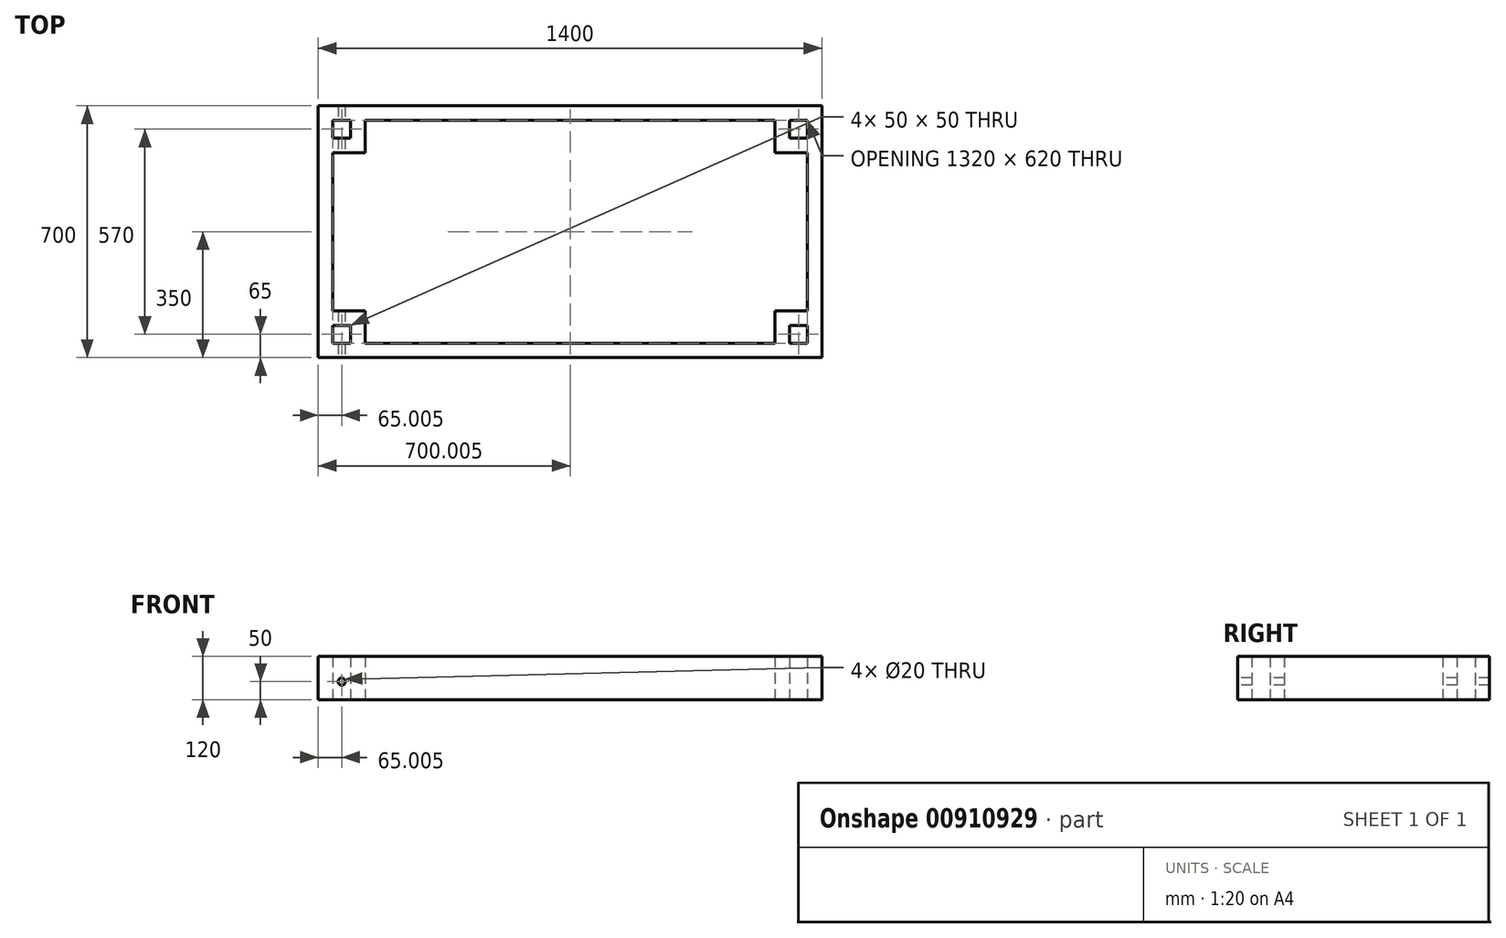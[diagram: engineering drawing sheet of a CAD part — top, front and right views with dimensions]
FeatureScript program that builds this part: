
annotation { "Feature Type Name" : "Feature", "Feature Type Description" : "" }
export const myFeature = defineFeature(function(context is Context, id is Id, definition is map)
    precondition{}
    {
        {
            var Q0;
            Q0=qCreatedBy(makeId("Top.planeOp"),FACE);
            var sketch = newSketch(context, id + "F0", { "sketchPlane" : qUnion([Q0])});
            skLineSegment(sketch, "E0.bottom", {"start": v(-2242.53, -660) * mm, "end": v(-842.53, -660) * mm});
            skLineSegment(sketch, "E0.top", {"start": v(-2242.53, 40) * mm, "end": v(-842.53, 40) * mm});
            skLineSegment(sketch, "E0.left", {"start": v(-2242.53, -660) * mm, "end": v(-2242.53, 40) * mm});
            skLineSegment(sketch, "E0.right", {"start": v(-842.53, -660) * mm, "end": v(-842.53, 40) * mm});
            skLineSegment(sketch, "E1.bottom", {"start": v(-2202.53, 0) * mm, "end": v(-2152.53, 0) * mm});
            skLineSegment(sketch, "E1.top", {"start": v(-2202.53, -620) * mm, "end": v(-2152.53, -620) * mm});
            skLineSegment(sketch, "E1.left", {"start": v(-2202.53, 0) * mm, "end": v(-2202.53, -50) * mm});
            skLineSegment(sketch, "E1.right", {"start": v(-882.53, 0) * mm, "end": v(-882.53, -50) * mm});
            skLineSegment(sketch, "E2.top", {"start": v(-2202.53, -50) * mm, "end": v(-2152.53, -50) * mm});
            skLineSegment(sketch, "E2.right", {"start": v(-2152.53, 0) * mm, "end": v(-2152.53, -50) * mm});
            skLineSegment(sketch, "E3.bottom", {"start": v(-932.53, 0) * mm, "end": v(-882.53, 0) * mm});
            skLineSegment(sketch, "E3.top", {"start": v(-932.53, -50) * mm, "end": v(-882.53, -50) * mm});
            skLineSegment(sketch, "E3.left", {"start": v(-932.53, 0) * mm, "end": v(-932.53, -50) * mm});
            skLineSegment(sketch, "E4.bottom", {"start": v(-932.53, -570) * mm, "end": v(-882.53, -570) * mm});
            skLineSegment(sketch, "E4.top", {"start": v(-932.53, -620) * mm, "end": v(-882.53, -620) * mm});
            skLineSegment(sketch, "E4.left", {"start": v(-932.53, -570) * mm, "end": v(-932.53, -620) * mm});
            skLineSegment(sketch, "E4.right", {"start": v(-882.53, -570) * mm, "end": v(-882.53, -620) * mm});
            skLineSegment(sketch, "E5.bottom", {"start": v(-2202.53, -570) * mm, "end": v(-2152.53, -570) * mm});
            skLineSegment(sketch, "E5.left", {"start": v(-2202.53, -570) * mm, "end": v(-2202.53, -620) * mm});
            skLineSegment(sketch, "E5.right", {"start": v(-2152.53, -570) * mm, "end": v(-2152.53, -620) * mm});
            skLineSegment(sketch, "E6.top", {"start": v(-2202.53, -90) * mm, "end": v(-2112.53, -90) * mm});
            skLineSegment(sketch, "E6.right", {"start": v(-2112.53, 0) * mm, "end": v(-2112.53, -90) * mm});
            skLineSegment(sketch, "E7.top", {"start": v(-2202.53, -530) * mm, "end": v(-2112.53, -530) * mm});
            skLineSegment(sketch, "E7.left", {"start": v(-2202.53, -620) * mm, "end": v(-2202.53, -570) * mm});
            skLineSegment(sketch, "E7.right", {"start": v(-2112.53, -620) * mm, "end": v(-2112.53, -530) * mm});
            skLineSegment(sketch, "E8.bottom", {"start": v(-882.53, 0) * mm, "end": v(-932.53, 0) * mm});
            skLineSegment(sketch, "E8.top", {"start": v(-882.53, -90) * mm, "end": v(-972.53, -90) * mm});
            skLineSegment(sketch, "E8.right", {"start": v(-972.53, 0) * mm, "end": v(-972.53, -90) * mm});
            skLineSegment(sketch, "E9.bottom", {"start": v(-882.53, -620) * mm, "end": v(-932.53, -620) * mm});
            skLineSegment(sketch, "E9.top", {"start": v(-882.53, -530) * mm, "end": v(-972.53, -530) * mm});
            skLineSegment(sketch, "E9.left", {"start": v(-882.53, -620) * mm, "end": v(-882.53, -570) * mm});
            skLineSegment(sketch, "E9.right", {"start": v(-972.53, -620) * mm, "end": v(-972.53, -530) * mm});
            skLineSegment(sketch, "E10.trimOffspring", {"start": v(-2202.53, -90) * mm, "end": v(-2202.53, -530) * mm});
            skLineSegment(sketch, "E11.trimOffspring", {"start": v(-2112.53, 0) * mm, "end": v(-972.53, 0) * mm});
            skLineSegment(sketch, "E12.trimOffspring", {"start": v(-2112.53, -620) * mm, "end": v(-972.53, -620) * mm});
            skLineSegment(sketch, "E13.trimOffspring", {"start": v(-882.53, -90) * mm, "end": v(-882.53, -530) * mm});
            skSolve(sketch);
        }
        {
            var Q0;
            Q0 = qSketchRegion(id + "F0", true);
            extrude(context, id + "F1", {"entities" : qUnion([Q0]), "depth" : 120 * mm, "offsetDistance" : 25 * mm});
        }
        {
            var Q0;
            Q0=makeQuery(id+"F1.opExtrude","SWEPT_FACE",FACE,{"disambiguationData":[OSD([sQuery(id+"F0.wireOp",EDGE,"E0.bottom")])]});
            var sketch = newSketch(context, id + "F2", { "sketchPlane" : qUnion([Q0])});
            skCircle(sketch, "E14", {"center": v(-2177.53, 50) * mm, "radius": 10 * mm});
            skSolve(sketch);
        }
        {
            var Q0;
            Q0 = qSketchRegion(id + "F2", true);
            extrude(context, id + "F3", {"entities" : qUnion([Q0]), "operationType" : NewBodyOperationType.REMOVE, "oppositeDirection" : true, "depth" : 1000 * mm, "offsetDistance" : 25 * mm});
        }
    });
